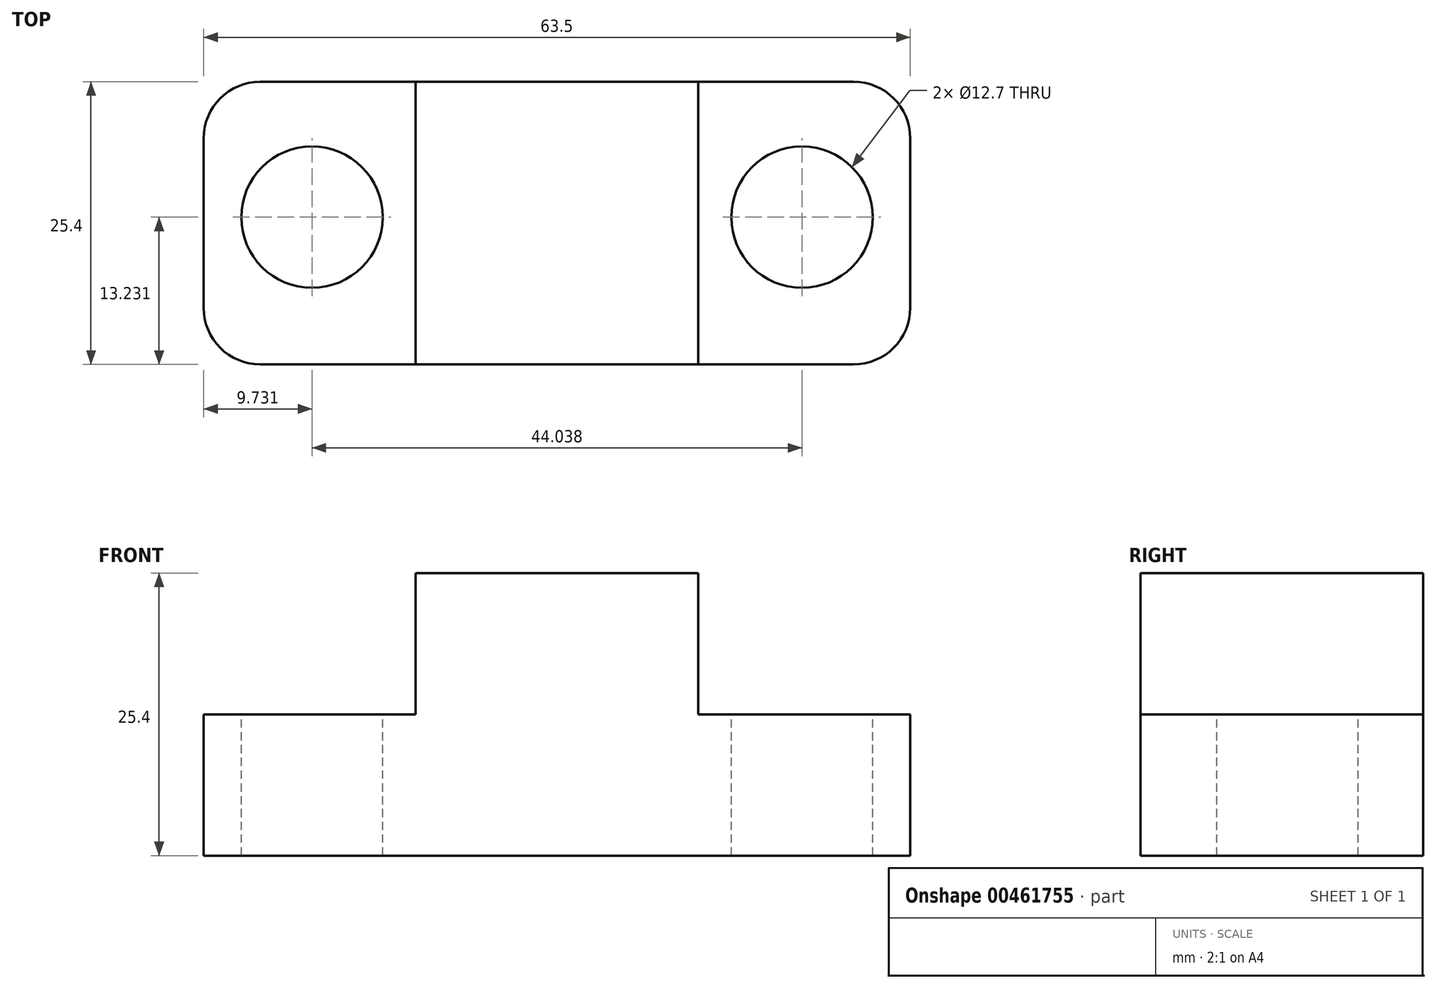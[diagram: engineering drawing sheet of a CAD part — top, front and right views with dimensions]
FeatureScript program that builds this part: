
annotation { "Feature Type Name" : "Feature", "Feature Type Description" : "" }
export const myFeature = defineFeature(function(context is Context, id is Id, definition is map)
    precondition{}
    {
        {
            var Q0;
            Q0=qCreatedBy(makeId("Front.planeOp"),FACE);
            var sketch = newSketch(context, id + "F0", { "sketchPlane" : qUnion([Q0])});
            skLineSegment(sketch, "E0", {"start": v(0, 0) * mm, "end": v(31.75, 0) * mm});
            skLineSegment(sketch, "E1", {"start": v(31.75, 0) * mm, "end": v(31.75, 25.4) * mm});
            skLineSegment(sketch, "E2", {"start": v(31.75, 25.4) * mm, "end": v(19.05, 25.4) * mm});
            skLineSegment(sketch, "E3", {"start": v(19.05, 25.4) * mm, "end": v(19.05, 12.7) * mm});
            skLineSegment(sketch, "E4", {"start": v(19.05, 12.7) * mm, "end": v(0, 12.7) * mm});
            skLineSegment(sketch, "E5", {"start": v(0, 12.7) * mm, "end": v(0, 0) * mm});
            skSolve(sketch);
        }
        {
            var Q0;
            Q0 = qSketchRegion(id + "F0", true);
            extrude(context, id + "F1", {"entities" : qUnion([Q0]), "depth" : 25.4 * mm});
        }
        {
            var Q0;
            Q0=makeQuery(id+"F1.opExtrude","CAP_EDGE",EDGE,{"disambiguationData":[OSD([sQuery(id+"F0.wireOp",EDGE,"E5")])],"isStart":false});
            fillet(context, id + "F2", {"entities" : qUnion([Q0]), "radius" : 5.08 * mm, "tangentPropagation" : true, "allowEdgeOverflow" : false});
        }
        {
            var Q0;
            Q0=makeQuery(id+"F1.opExtrude","CAP_EDGE",EDGE,{"disambiguationData":[OSD([sQuery(id+"F0.wireOp",EDGE,"E5")])],"isStart":true});
            fillet(context, id + "F3", {"entities" : qUnion([Q0]), "radius" : 5.08 * mm, "tangentPropagation" : true, "allowEdgeOverflow" : false});
        }
        {
            var Q0;
            Q0=makeQuery(id+"F1.opExtrude","SWEPT_FACE",FACE,{"disambiguationData":[OSD([sQuery(id+"F0.wireOp",EDGE,"E4")])]});
            var sketch = newSketch(context, id + "F4", { "sketchPlane" : qUnion([Q0])});
            skCircle(sketch, "E6", {"center": v(9.73, -12.17) * mm, "radius": 5.27 * mm});
            skSolve(sketch);
        }
        {
            var Q0;
            Q0=sQuery(id+"F4.wireOp",VERTEX,"E6.center");
            var Q1;
            Q1=makeQuery(id+"F1.opExtrude","SWEPT_BODY",BODY,{"disambiguationData":[OSD([sQuery(id+"F0.wireOp",EDGE,"E0"),sQuery(id+"F0.wireOp",EDGE,"E1"),sQuery(id+"F0.wireOp",EDGE,"E2"),sQuery(id+"F0.wireOp",EDGE,"E3"),sQuery(id+"F0.wireOp",EDGE,"E4"),sQuery(id+"F0.wireOp",EDGE,"E5")])]});
            hole(context, id + "F5", {"style" : HoleStyle.SIMPLE, "endStyle" : HoleEndStyle.THROUGH, "holeDiameter" : 12.7 * mm, "isTappedThrough" : true, "tappedDepth" : 12.7 * mm, "tapClearance" : 3, "locations" : qUnion([Q0]), "scope" : qUnion([Q1])});
        }
        {
            var Q0;
            Q0=makeQuery(id+"F1.opExtrude","SWEPT_BODY",BODY,{"disambiguationData":[OSD([sQuery(id+"F0.wireOp",EDGE,"E0"),sQuery(id+"F0.wireOp",EDGE,"E1"),sQuery(id+"F0.wireOp",EDGE,"E2"),sQuery(id+"F0.wireOp",EDGE,"E3"),sQuery(id+"F0.wireOp",EDGE,"E4"),sQuery(id+"F0.wireOp",EDGE,"E5")])]});
            var Q1;
            Q1=makeQuery(id+"F1.opExtrude","SWEPT_FACE",FACE,{"disambiguationData":[OSD([sQuery(id+"F0.wireOp",EDGE,"E1")])]});
            mirror(context, id + "F6", {"operationType" : NewBodyOperationType.ADD, "entities" : qUnion([Q0]), "mirrorPlane" : qUnion([Q1])});
        }
    });
